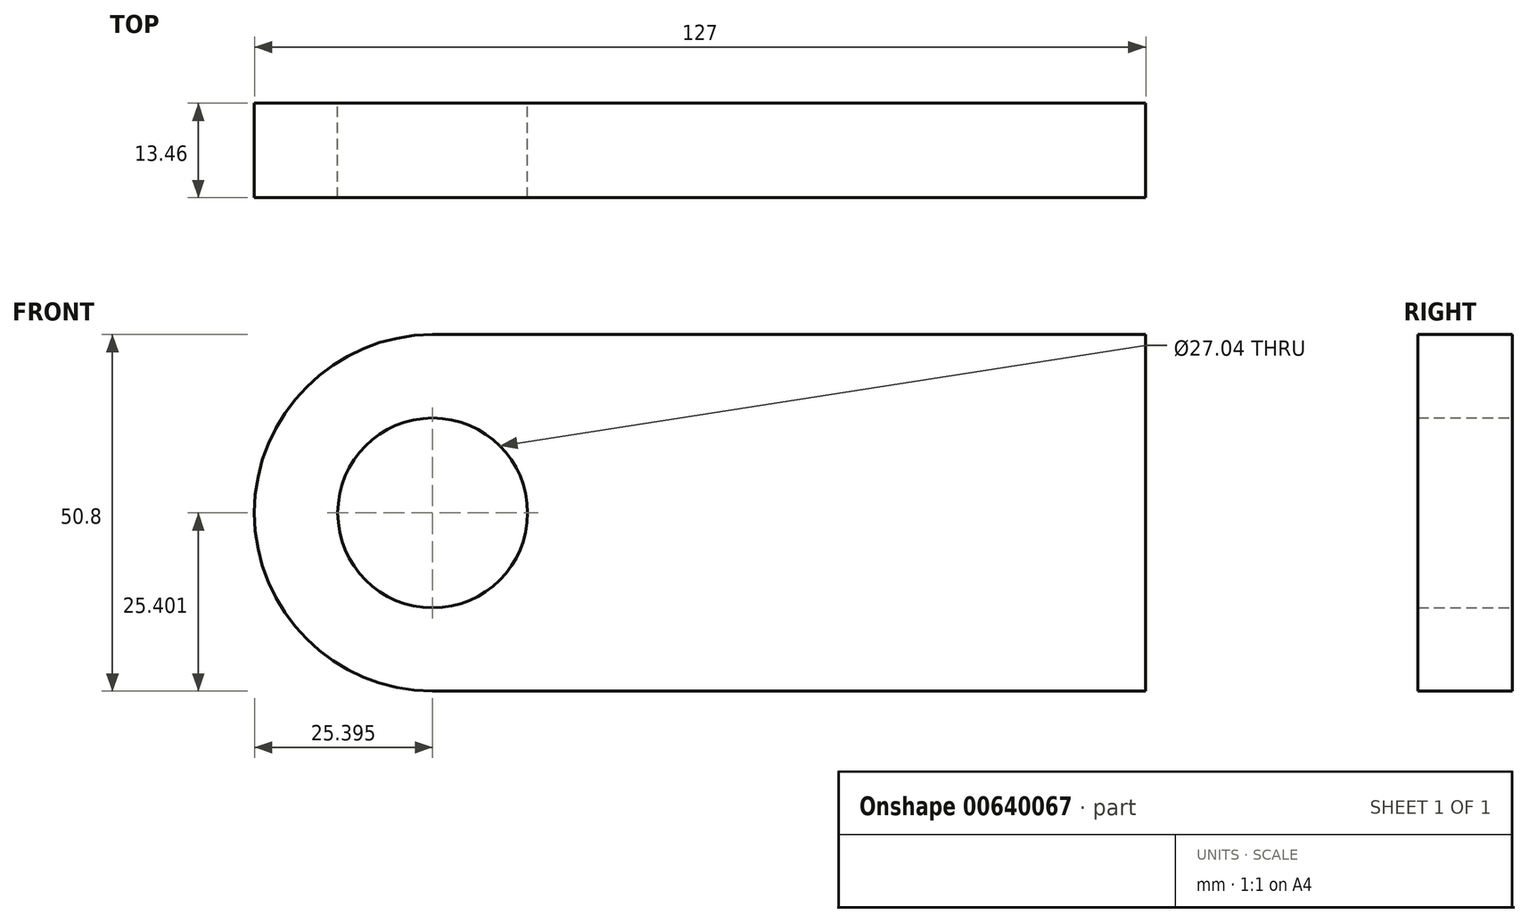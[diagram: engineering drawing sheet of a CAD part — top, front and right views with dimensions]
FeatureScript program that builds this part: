
annotation { "Feature Type Name" : "Feature", "Feature Type Description" : "" }
export const myFeature = defineFeature(function(context is Context, id is Id, definition is map)
    precondition{}
    {
        {
            var Q0;
            Q0=qCreatedBy(makeId("Front.planeOp"),FACE);
            var sketch = newSketch(context, id + "F0", { "sketchPlane" : qUnion([Q0])});
            skLineSegment(sketch, "E0.bottom", {"start": v(-42.96, -30.32) * mm, "end": v(58.64, -30.32) * mm});
            skLineSegment(sketch, "E0.top", {"start": v(-42.96, 20.48) * mm, "end": v(58.64, 20.48) * mm});
            skLineSegment(sketch, "E0.left", {"start": v(-42.96, -30.32) * mm, "end": v(-42.96, 20.48) * mm});
            skLineSegment(sketch, "E0.right", {"start": v(58.64, -30.32) * mm, "end": v(58.64, 20.48) * mm});
            skArc(sketch, "E1", {"start": v(-42.96, 20.48) * mm, "mid": v(-68.36, -4.92) * mm, "end": v(-42.96, -30.32) * mm});
            skCircle(sketch, "E2", {"center": v(-42.96, -4.92) * mm, "radius": 13.52 * mm});
            skSolve(sketch);
        }
        {
            var Q0;
            Q0=makeQuery(id+"F0.imprint","IMPRINT",FACE,{"disambiguationData":[TD([[makeQuery(id+"F0.imprint","IMPRINT",EDGE,{"derivedFrom":sQuery(id+"F0.wireOp",EDGE,"E0.bottom")}),1.0]])]});
            var sketch = newSketch(context, id + "F1", { "sketchPlane" : qUnion([Q0])});
            skSolve(sketch);
        }
        {
            var Q0;
            Q0=makeQuery(id+"F0.imprint","IMPRINT",FACE,{"disambiguationData":[TD([[makeQuery(id+"F0.imprint","IMPRINT",EDGE,{"derivedFrom":sQuery(id+"F0.wireOp",EDGE,"E0.bottom")}),1.0]])]});
            var Q1;
            {var subQ0=sQuery(id+"F0.wireOp",EDGE,"E1");Q1=makeQuery(id+"F0.imprint","IMPRINT",FACE,{"disambiguationData":[TD([[makeQuery(id+"F0.imprint","IMPRINT",EDGE,{"derivedFrom":subQ0}),1.0]])]});}
            extrude(context, id + "F2", {"entities" : qUnion([Q0, Q1]), "depth" : 13.46 * mm, "offsetDistance" : 25.4 * mm});
        }
    });
